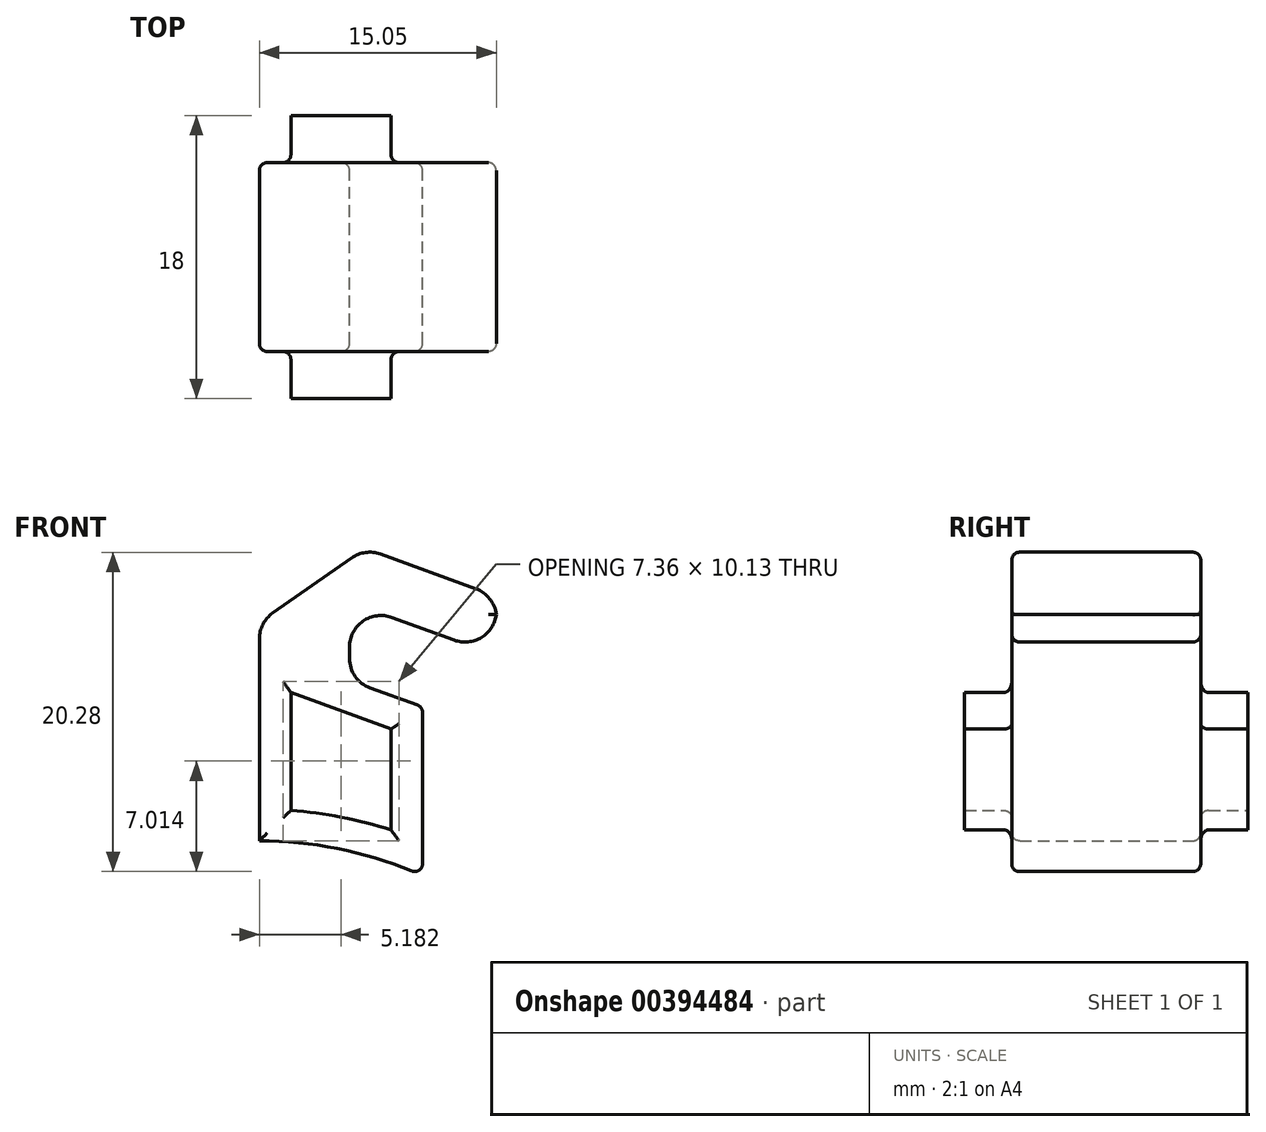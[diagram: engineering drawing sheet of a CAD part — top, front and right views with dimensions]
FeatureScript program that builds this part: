
annotation { "Feature Type Name" : "Feature", "Feature Type Description" : "" }
export const myFeature = defineFeature(function(context is Context, id is Id, definition is map)
    precondition{}
    {
        {
            var Q0;
            Q0=qCreatedBy(makeId("Front.planeOp"),FACE);
            var sketch = newSketch(context, id + "F0", { "sketchPlane" : qUnion([Q0])});
            skLineSegment(sketch, "E0.5", {"start": v(2, 34.82) * mm, "end": v(8.36, 32.5) * mm});
            skLineSegment(sketch, "E1", {"start": v(0, 25.4) * mm, "end": v(0, 37.67) * mm});
            skArc(sketch, "E2.trimOffspring", {"start": v(8.36, 26.1) * mm, "mid": v(5.22, 26.9) * mm, "end": v(2, 27.33) * mm});
            skLineSegment(sketch, "E3", {"start": v(2, 34.82) * mm, "end": v(2, 27.33) * mm});
            skLineSegment(sketch, "E4", {"start": v(10.36, 25.36) * mm, "end": v(10.36, 23.19) * mm});
            skLineSegment(sketch, "E5", {"start": v(10.36, 25.36) * mm, "end": v(10.36, 33.9) * mm});
            skArc(sketch, "E6.trimOffspring", {"start": v(10.36, 23.19) * mm, "mid": v(5.3, 24.84) * mm, "end": v(0, 25.4) * mm});
            skLineSegment(sketch, "E7", {"start": v(8.36, 32.5) * mm, "end": v(8.36, 26.1) * mm});
            skLineSegment(sketch, "E8", {"start": v(0, 37.67) * mm, "end": v(0, 40.28) * mm});
            skPoint(sketch, "E9.start.orphan", {"position": v(3.76, 36.3) * mm});
            skLineSegment(sketch, "E10.trimOffspring", {"start": v(7.52, 34.94) * mm, "end": v(10.36, 33.9) * mm});
            skLineSegment(sketch, "E11", {"start": v(0, 37.67) * mm, "end": v(7.52, 34.94) * mm});
            skLineSegment(sketch, "E12", {"start": v(0, 46.41) * mm, "end": v(0, 40.28) * mm});
            skLineSegment(sketch, "E13", {"start": v(15.06, 40.93) * mm, "end": v(15.06, 37.17) * mm});
            skLineSegment(sketch, "E14", {"start": v(0, 46.41) * mm, "end": v(15.06, 40.93) * mm});
            skLineSegment(sketch, "E15", {"start": v(15.06, 37.17) * mm, "end": v(5.72, 40.57) * mm});
            skLineSegment(sketch, "E16", {"start": v(3.84, 36.25) * mm, "end": v(5.72, 35.59) * mm});
            skLineSegment(sketch, "E17", {"start": v(5.72, 40.57) * mm, "end": v(5.72, 35.59) * mm});
            skSolve(sketch);
        }
        {
            var Q0;
            {var subQ2=sQuery(id+"F0.wireOp",EDGE,"E8");Q0=makeQuery(id+"F0.imprint","IMPRINT",FACE,{"disambiguationData":[TD([[makeQuery(id+"F0.imprint","IMPRINT",EDGE,{"derivedFrom":subQ2}),-1.0]])]});}
            var Q1;
            Q1=makeQuery(id+"F0.imprint","IMPRINT",FACE,{"disambiguationData":[TD([[makeQuery(id+"F0.imprint","IMPRINT",EDGE,{"derivedFrom":sQuery(id+"F0.wireOp",EDGE,"E0.5")}),1.0]])]});
            extrude(context, id + "F1", {"entities" : qUnion([Q0, Q1]), "endBound" : BoundingType.SYMMETRIC, "depth" : 12 * mm});
        }
        {
            var Q0;
            Q0=makeQuery(id+"F0.imprint","IMPRINT",FACE,{"disambiguationData":[TD([[makeQuery(id+"F0.imprint","IMPRINT",EDGE,{"derivedFrom":sQuery(id+"F0.wireOp",EDGE,"E0.5")}),-1.0]])]});
            extrude(context, id + "F2", {"entities" : qUnion([Q0]), "operationType" : NewBodyOperationType.ADD, "endBound" : BoundingType.SYMMETRIC, "depth" : 18 * mm});
        }
        {
            var Q0;
            Q0=makeQuery(id+"F1.opExtrude","SWEPT_EDGE",EDGE,{"disambiguationData":[OSD([sQuery(id+"F0.wireOp",EDGE,"E12"),sQuery(id+"F0.wireOp",EDGE,"E14")])]});
            chamfer(context, id + "F3", {"entities" : qUnion([Q0]), "width" : 5 * mm, "tangentPropagation" : true});
        }
        {
            var Q0;
            Q0=makeQuery(id+"F1.opExtrude","SWEPT_EDGE",EDGE,{"disambiguationData":[OSD([sQuery(id+"F0.wireOp",EDGE,"E15"),sQuery(id+"F0.wireOp",EDGE,"E17")])]});
            var Q1;
            Q1=makeQuery(id+"F1.opExtrude","SWEPT_EDGE",EDGE,{"disambiguationData":[OSD([sQuery(id+"F0.wireOp",EDGE,"E11"),sQuery(id+"F0.wireOp",EDGE,"E17")])]});
            fillet(context, id + "F4", {"entities" : qUnion([Q0, Q1]), "radius" : 2 * mm, "tangentPropagation" : true, "allowEdgeOverflow" : false});
        }
        {
            var Q0;
            {var subQ0=sQuery(id+"F0.wireOp",EDGE,"E14");Q0=makeQuery(id+"F3.opChamfer","BLEND_EDGE",EDGE,{"blendedFrom":[makeQuery(id+"F1.opExtrude","SWEPT_EDGE",EDGE,{"disambiguationData":[OSD([sQuery(id+"F0.wireOp",EDGE,"E12"),subQ0])]}),makeQuery(id+"F1.opExtrude","SWEPT_FACE",FACE,{"disambiguationData":[OSD([subQ0])]})],"blendedInto":[makeQuery(id+"F1.opExtrude","SWEPT_FACE",FACE,{"disambiguationData":[OSD([subQ0])]})]});}
            var Q1;
            {var subQ0=sQuery(id+"F0.wireOp",EDGE,"E12");Q1=makeQuery(id+"F3.opChamfer","BLEND_EDGE",EDGE,{"blendedFrom":[makeQuery(id+"F1.opExtrude","SWEPT_EDGE",EDGE,{"disambiguationData":[OSD([subQ0,sQuery(id+"F0.wireOp",EDGE,"E14")])]}),makeQuery(id+"F1.opExtrude","SWEPT_FACE",FACE,{"disambiguationData":[OSD([sQuery(id+"F0.wireOp",EDGE,"E1"),sQuery(id+"F0.wireOp",EDGE,"E8"),subQ0])]})],"blendedInto":[makeQuery(id+"F1.opExtrude","SWEPT_FACE",FACE,{"disambiguationData":[OSD([sQuery(id+"F0.wireOp",EDGE,"E1"),sQuery(id+"F0.wireOp",EDGE,"E8"),subQ0])]})]});}
            var Q2;
            Q2=makeQuery(id+"F1.opExtrude","SWEPT_EDGE",EDGE,{"disambiguationData":[OSD([sQuery(id+"F0.wireOp",EDGE,"E13"),sQuery(id+"F0.wireOp",EDGE,"E15")])]});
            var Q3;
            Q3=makeQuery(id+"F1.opExtrude","SWEPT_EDGE",EDGE,{"disambiguationData":[OSD([sQuery(id+"F0.wireOp",EDGE,"E13"),sQuery(id+"F0.wireOp",EDGE,"E14")])]});
            fillet(context, id + "F5", {"entities" : qUnion([Q0, Q1, Q2, Q3]), "radius" : 2 * mm, "tangentPropagation" : true, "allowEdgeOverflow" : false});
        }
        {
            var Q0;
            Q0=makeQuery(id+"F1.opExtrude","CAP_FACE",FACE,{"disambiguationData":[OSD([sQuery(id+"F0.wireOp",EDGE,"E0.5"),sQuery(id+"F0.wireOp",EDGE,"E1"),sQuery(id+"F0.wireOp",EDGE,"E2.trimOffspring"),sQuery(id+"F0.wireOp",EDGE,"E3"),sQuery(id+"F0.wireOp",EDGE,"E4"),sQuery(id+"F0.wireOp",EDGE,"E5"),sQuery(id+"F0.wireOp",EDGE,"E6.trimOffspring"),sQuery(id+"F0.wireOp",EDGE,"E7"),sQuery(id+"F0.wireOp",EDGE,"E8"),sQuery(id+"F0.wireOp",EDGE,"E10.trimOffspring"),sQuery(id+"F0.wireOp",EDGE,"E11"),sQuery(id+"F0.wireOp",EDGE,"E12"),sQuery(id+"F0.wireOp",EDGE,"E13"),sQuery(id+"F0.wireOp",EDGE,"E14"),sQuery(id+"F0.wireOp",EDGE,"E15"),sQuery(id+"F0.wireOp",EDGE,"E17")])],"isStart":false});
            var Q1;
            Q1=makeQuery(id+"F1.opExtrude","SWEPT_FACE",FACE,{"disambiguationData":[OSD([sQuery(id+"F0.wireOp",EDGE,"E4"),sQuery(id+"F0.wireOp",EDGE,"E5")])]});
            var Q2;
            Q2=makeQuery(id+"F1.opExtrude","CAP_FACE",FACE,{"disambiguationData":[OSD([sQuery(id+"F0.wireOp",EDGE,"E0.5"),sQuery(id+"F0.wireOp",EDGE,"E1"),sQuery(id+"F0.wireOp",EDGE,"E2.trimOffspring"),sQuery(id+"F0.wireOp",EDGE,"E3"),sQuery(id+"F0.wireOp",EDGE,"E4"),sQuery(id+"F0.wireOp",EDGE,"E5"),sQuery(id+"F0.wireOp",EDGE,"E6.trimOffspring"),sQuery(id+"F0.wireOp",EDGE,"E7"),sQuery(id+"F0.wireOp",EDGE,"E8"),sQuery(id+"F0.wireOp",EDGE,"E10.trimOffspring"),sQuery(id+"F0.wireOp",EDGE,"E11"),sQuery(id+"F0.wireOp",EDGE,"E12"),sQuery(id+"F0.wireOp",EDGE,"E13"),sQuery(id+"F0.wireOp",EDGE,"E14"),sQuery(id+"F0.wireOp",EDGE,"E15"),sQuery(id+"F0.wireOp",EDGE,"E17")])],"isStart":true});
            fillet(context, id + "F6", {"entities" : qUnion([Q0, Q1, Q2]), "radius" : .5 * mm, "tangentPropagation" : true, "allowEdgeOverflow" : false});
        }
    });
